FCSTD DOCUMENT  (FreeCAD 1.0R39109 (Git))
Label: joy
License: All rights reserved
LicenseURL: https://en.wikipedia.org/wiki/All_rights_reserved
objects: Sketcher::SketchObject×1, PartDesign::Body×1
note: 3 computed .brp shape members not serialized (recipe doc carries the construction recipe); baked Part::Feature solids carry a one-line shape summary decoded from their .brp

FEATURE [Sketcher::SketchObject] Sketch
  ArcFitTolerance = 1e-06
  AttachmentSupport = -> [XY_Plane]
  FullyConstrained = false
  MakeInternals = false
  MapMode = 5
  sketch-geometry (51):
    g0: LineSegment StartX=70 StartY=4.02596e-07 StartZ=0 EndX=70 EndY=26 EndZ=0
    g1: LineSegment StartX=-70 StartY=26 StartZ=0 EndX=-70 EndY=0 EndZ=0
    g2: LineSegment StartX=-70 StartY=0 StartZ=0 EndX=-70 EndY=-56 EndZ=0
    g3: LineSegment StartX=-66 StartY=-60 StartZ=0 EndX=-44 EndY=-60 EndZ=0
    g4: LineSegment StartX=-40 StartY=-56 StartZ=0 EndX=-40 EndY=2.26455e-07 EndZ=0
    g5: LineSegment StartX=40 StartY=2.26455e-07 StartZ=0 EndX=40 EndY=-56 EndZ=0
    g6: LineSegment StartX=44 StartY=-60 StartZ=0 EndX=66 EndY=-60 EndZ=0
    g7: LineSegment StartX=70 StartY=-56 StartZ=0 EndX=70 EndY=4.02596e-07 EndZ=0
    g8: ArcOfCircle CenterX=-66 CenterY=26 CenterZ=0 NormalX=0 NormalY=0 NormalZ=1 AngleXU=0 Radius=4.00003 StartAngle=1.57081 EndAngle=3.14159
    g9: GeomPoint [constr] X=-70 Y=30 Z=0
    g10: ArcOfCircle CenterX=66 CenterY=26 CenterZ=0 NormalX=0 NormalY=0 NormalZ=1 AngleXU=0 Radius=4 StartAngle=0 EndAngle=1.5708
    g11: GeomPoint [constr] X=70 Y=30 Z=0
    g12: ArcOfCircle CenterX=66 CenterY=-56 CenterZ=0 NormalX=0 NormalY=0 NormalZ=1 AngleXU=0 Radius=4 StartAngle=4.71239 EndAngle=6.28319
    g13: GeomPoint [constr] X=70 Y=-60 Z=0
    g14: ArcOfCircle CenterX=-66 CenterY=-56 CenterZ=0 NormalX=0 NormalY=0 NormalZ=1 AngleXU=0 Radius=4 StartAngle=3.14159 EndAngle=4.71239
    g15: GeomPoint [constr] X=-70 Y=-60 Z=0
    g16: ArcOfCircle CenterX=-44 CenterY=-56 CenterZ=0 NormalX=0 NormalY=0 NormalZ=1 AngleXU=0 Radius=4 StartAngle=4.71239 EndAngle=6.28319
    g17: GeomPoint [constr] X=-40 Y=-60 Z=0
    g18: LineSegment StartX=-40 StartY=2.26455e-07 StartZ=0 EndX=40 EndY=2.26455e-07 EndZ=0
    g19: ArcOfCircle CenterX=44 CenterY=-56 CenterZ=0 NormalX=0 NormalY=0 NormalZ=1 AngleXU=0 Radius=4 StartAngle=3.14159 EndAngle=4.71239
    g20: GeomPoint [constr] X=40 Y=-60 Z=0
    g21: Circle CenterX=-55 CenterY=-40 CenterZ=0 NormalX=0 NormalY=0 NormalZ=1 AngleXU=0 Radius=6.5
    g22: Circle CenterX=-55 CenterY=-10 CenterZ=0 NormalX=0 NormalY=0 NormalZ=1 AngleXU=0 Radius=6.5
    g23: Circle CenterX=-17 CenterY=15 CenterZ=0 NormalX=0 NormalY=0 NormalZ=1 AngleXU=0 Radius=6.5
    g24: Circle CenterX=0 CenterY=15 CenterZ=0 NormalX=0 NormalY=0 NormalZ=1 AngleXU=0 Radius=6.5
    g25: Circle CenterX=17 CenterY=15 CenterZ=0 NormalX=0 NormalY=0 NormalZ=1 AngleXU=0 Radius=6.5
    g26: Circle CenterX=55 CenterY=-10 CenterZ=0 NormalX=0 NormalY=0 NormalZ=1 AngleXU=0 Radius=6.5
    g27: Circle CenterX=55 CenterY=-40 CenterZ=0 NormalX=0 NormalY=0 NormalZ=1 AngleXU=0 Radius=6.5
    g28: LineSegment StartX=66 StartY=30 StartZ=0 EndX=66 EndY=52 EndZ=0
    g29: LineSegment StartX=62 StartY=56 StartZ=0 EndX=26 EndY=56 EndZ=0
    g30: LineSegment StartX=-66 StartY=52 StartZ=0 EndX=-66 EndY=30 EndZ=0
    g31: ArcOfCircle CenterX=-61.9722 CenterY=52 CenterZ=0 NormalX=0 NormalY=0 NormalZ=1 AngleXU=0 Radius=4.02778 StartAngle=1.45328 EndAngle=3.14159
    g32: GeomPoint [constr] X=-66 Y=56 Z=0
    g33: ArcOfCircle CenterX=62 CenterY=52 CenterZ=0 NormalX=0 NormalY=0 NormalZ=1 AngleXU=0 Radius=4 StartAngle=7e-16 EndAngle=1.5708
    g34: GeomPoint [constr] X=66 Y=56 Z=0
    g35: LineSegment StartX=-21.5 StartY=52 StartZ=0 EndX=-21.5 EndY=30 EndZ=0
    g36: LineSegment StartX=22 StartY=30 StartZ=0 EndX=22 EndY=52 EndZ=0
    g37: LineSegment StartX=-25.5 StartY=56 StartZ=0 EndX=-61.5 EndY=56 EndZ=0
    g38: ArcOfCircle CenterX=-25.5 CenterY=52 CenterZ=0 NormalX=0 NormalY=0 NormalZ=1 AngleXU=0 Radius=4 StartAngle=0 EndAngle=1.5708
    g39: ArcOfCircle CenterX=26 CenterY=52 CenterZ=0 NormalX=0 NormalY=0 NormalZ=1 AngleXU=0 Radius=4 StartAngle=1.5708 EndAngle=3.14159
    g40: Circle CenterX=-55 CenterY=43 CenterZ=0 NormalX=0 NormalY=0 NormalZ=1 AngleXU=0 Radius=6.5
    g41: Circle CenterX=55 CenterY=43 CenterZ=0 NormalX=0 NormalY=0 NormalZ=1 AngleXU=0 Radius=6.5
    g42: LineSegment StartX=22 StartY=52 StartZ=0 EndX=22 EndY=78 EndZ=0
    g43: LineSegment StartX=18 StartY=82 StartZ=0 EndX=-17.5 EndY=82 EndZ=0
    g44: LineSegment StartX=-21.5 StartY=78 StartZ=0 EndX=-21.5 EndY=52 EndZ=0
    g45: ArcOfCircle CenterX=-17.5 CenterY=78 CenterZ=0 NormalX=0 NormalY=0 NormalZ=1 AngleXU=0 Radius=4 StartAngle=1.5708 EndAngle=3.14159
    g46: GeomPoint [constr] X=-21.5 Y=82 Z=0
    g47: ArcOfCircle CenterX=18 CenterY=78 CenterZ=0 NormalX=0 NormalY=0 NormalZ=1 AngleXU=0 Radius=4 StartAngle=1.8e-15 EndAngle=1.5708
    g48: GeomPoint [constr] X=22 Y=82 Z=0
    g49: Circle CenterX=-35 CenterY=43 CenterZ=0 NormalX=0 NormalY=0 NormalZ=1 AngleXU=0 Radius=6.5
    g50: Circle CenterX=35 CenterY=43 CenterZ=0 NormalX=0 NormalY=0 NormalZ=1 AngleXU=0 Radius=6.5
  constraints (128):
    c: Vertical(g0)
    c: Vertical(g1)
    c: Distance(g0,g1) = 140
    c: Distance(g1,g9) = 30
    c: PointOnObject(g1,g-1)
    c: DistanceX(g1,g-1) = 70
    c: Vertical(g2)
    c: Vertical(g4)
    c: Horizontal(g3)
    c: Distance(g2,g4) = 30
    c: Distance(g15,g2) = 60
    c: Coincident(g2,g1)
    c: Horizontal(g6)
    c: Vertical(g5)
    c: Vertical(g7)
    c: Distance(g5,g7) = 30
    c: Distance(g7,g13) = 60
    c: PointOnObject(g9,g1)
    c: Tangent(g1,g8) = -1.5708
    c: PointOnObject(g11,g0)
    c: Tangent(g0,g10) = -1.5708
    c: PointOnObject(g13,g6)
    c: PointOnObject(g13,g7)
    c: Tangent(g6,g12) = -1.5708
    c: Tangent(g7,g12) = -1.5708
    c: PointOnObject(g15,g2)
    c: PointOnObject(g15,g3)
    c: Tangent(g2,g14) = -1.5708
    c: Tangent(g3,g14) = -1.5708
    c: PointOnObject(g17,g3)
    c: PointOnObject(g17,g4)
    c: Tangent(g3,g16) = -1.5708
    c: Tangent(g4,g16) = -1.5708
    c: Coincident(g18,g4)
    c: Horizontal(g18)
    c: DistanceY(g3,g16) = 4
    c: DistanceY(g3,g14) = 4
    c: DistanceY(g8,g30) = 4
    c: DistanceY(g10,g10) = 4
    c: DistanceY(g6,g12) = 4
    c: PointOnObject(g20,g6)
    c: PointOnObject(g20,g5)
    c: Tangent(g6,g19) = -1.5708
    c: Tangent(g5,g19) = -1.5708
    c: DistanceY(g6,g19) = 4
    c: DistanceX(g18,g18) = 80
    c: DistanceX(g30,g10) = 132
    c: Coincident(g7,g0)
    c: Coincident(g18,g5)
    c: Diameter(g21) = 13
    c: Diameter(g22) = 13
    c: Diameter(g23) = 13
    c: Diameter(g24) = 13
    c: PointOnObject(g24,g-2)
    c: Diameter(g25) = 13
    c: Diameter(g26) = 13
    c: Diameter(g27) = 13
    c: DistanceY(g25,g24) = 0
    c: DistanceY(g23,g24) = 0
    c: DistanceY(g22,g4) = 10
    c: DistanceY(g21,g22) = 30
    c: DistanceY(g22,g26) = 0
    c: DistanceY(g27,g21) = 0
    c: DistanceX(g23,g4) = -23
    c: DistanceX(g5,g25) = -23
    c: DistanceX(g5,g26) = 15
    c: DistanceX(g27,g26) = 0
    c: DistanceX(g22,g4) = 15
    c: DistanceX(g21,g22) = 0
    c: DistanceY(g-1,g24) = 15
    c: Horizontal(g29)
    c: Vertical(g28)
    c: Vertical(g30)
    c: PointOnObject(g32,g37)
    c: PointOnObject(g32,g30)
    c: Coincident(g37,g31) = -1.5708
    c: Tangent(g30,g31) = -1.5708
    c: PointOnObject(g34,g28)
    c: PointOnObject(g34,g29)
    c: Tangent(g28,g33) = -1.5708
    c: Tangent(g29,g33) = -1.5708
    c: DistanceY(g33,g29) = 4
    c: DistanceY(g31,g37) = 4
    c: DistanceY(g30,g30) = 22
    c: Vertical(g35)
    c: Vertical(g36)
    c: Tangent(g35,g38) = 1.5708
    c: Tangent(g37,g38) = -1.5708
    c: Tangent(g36,g39) = 1.5708
    c: Tangent(g29,g39) = -1.5708
    c: DistanceY(g39,g29) = 4
    c: DistanceX(g37,g37) = 36
    c: DistanceX(g29,g29) = 36
    c: DistanceY(g35,g35) = 22
    c: DistanceY(g38,g37) = 4
    c: DistanceY(g36,g36) = 22
    c: DistanceX(g8,g31) = 4.5
    c: Diameter(g40) = 13
    c: Diameter(g41) = 13
    c: DistanceX(g26,g41) = 0
    c: DistanceX(g22,g40) = 0
    c: DistanceY(g40,g31) = 9
    c: DistanceY(g41,g33) = 9
    c: Horizontal(g43)
    c: Vertical(g42)
    c: Vertical(g44)
    c: DistanceY(g42,g48) = 30
    c: PointOnObject(g46,g43)
    c: PointOnObject(g46,g44)
    c: Tangent(g43,g45) = -1.5708
    c: Tangent(g44,g45) = -1.5708
    c: PointOnObject(g48,g42)
    c: PointOnObject(g48,g43)
    c: Tangent(g42,g47) = -1.5708
    c: Tangent(g43,g47) = -1.5708
    c: DistanceY(g47,g43) = 4
    c: DistanceY(g45,g43) = 4
    c: Diameter(g49) = 13
    c: Diameter(g50) = 13
    c: DistanceY(g49,g40) = 0
    c: DistanceY(g28,g28) = 22
    c: DistanceY(g0,g0) = 26
    c: DistanceX(g10,g10) = 0
    c: DistanceX(g28,g10) = 0
    c: DistanceY(g10,g28) = 0
    c: DistanceY(g50,g41) = 0
    c: DistanceX(g50,g41) = 20
    c: DistanceX(g40,g49) = 20
FEATURE [PartDesign::Body] Body
  AllowCompound = false
  Group = -> [Sketch]
  Origin = -> Origin
